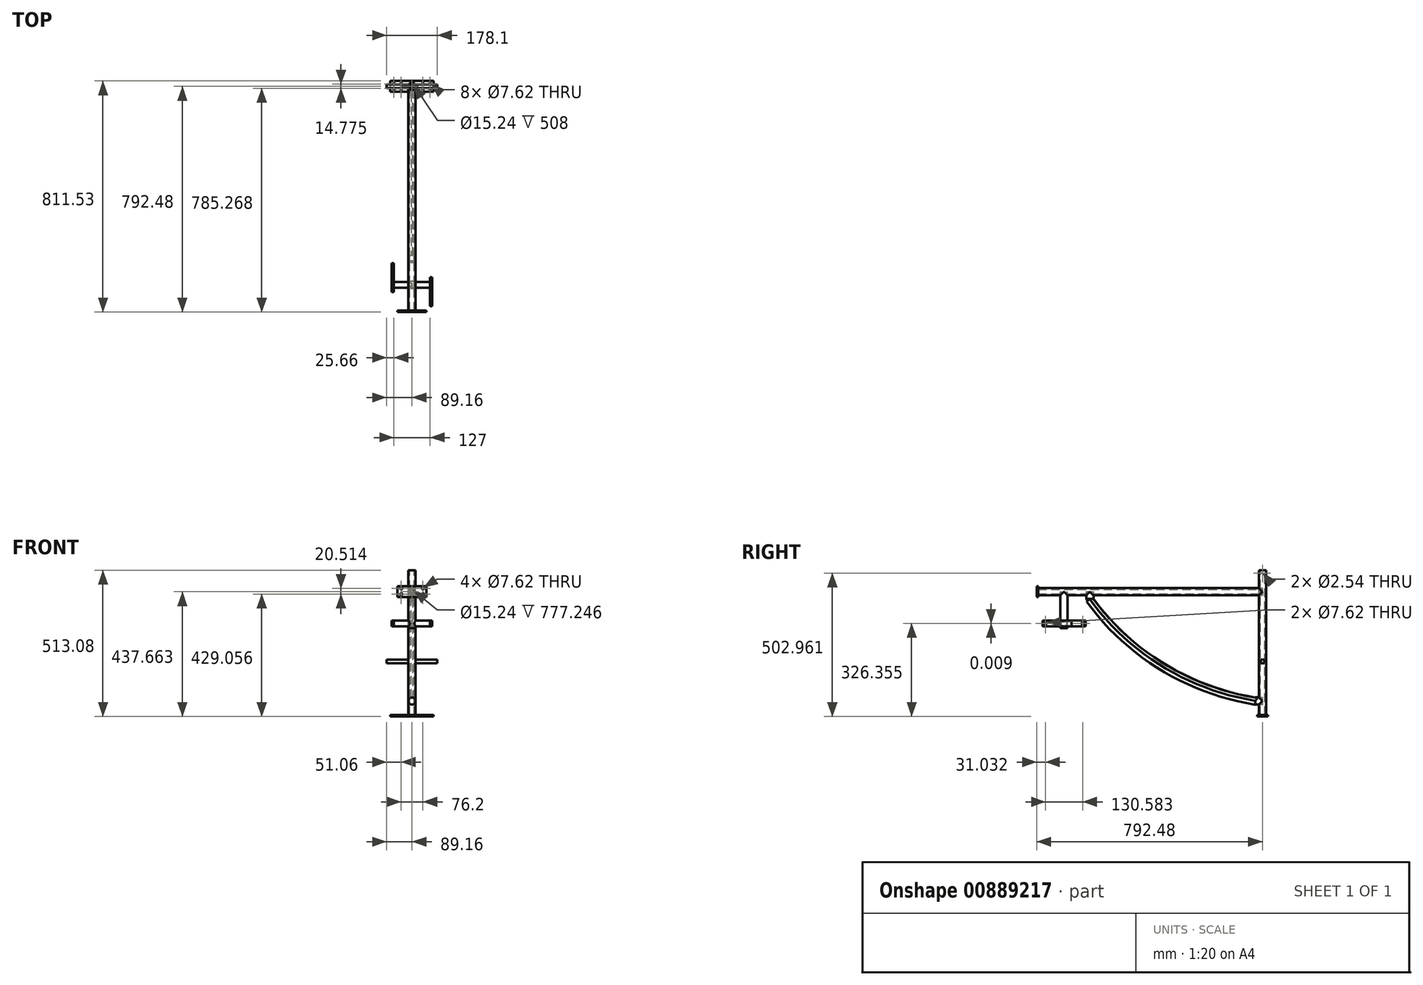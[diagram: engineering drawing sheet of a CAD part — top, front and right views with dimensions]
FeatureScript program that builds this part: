
annotation { "Feature Type Name" : "Feature", "Feature Type Description" : "" }
export const myFeature = defineFeature(function(context is Context, id is Id, definition is map)
    precondition{}
    {
        {
            var Q0;
            Q0=qCreatedBy(makeId("Top.planeOp"),FACE);
            var sketch = newSketch(context, id + "F0", { "sketchPlane" : qUnion([Q0])});
            skCircle(sketch, "E0", {"center": v(0, 0) * mm, "radius": 12.7 * mm});
            skCircle(sketch, "E1", {"center": v(0, 0) * mm, "radius": 7.62 * mm});
            skSolve(sketch);
        }
        {
            var Q0;
            Q0 = qSketchRegion(id + "F0", true);
            extrude(context, id + "F1", {"entities" : qUnion([Q0]), "oppositeDirection" : true, "depth" : 508 * mm, "offsetDistance" : 25.4 * mm});
        }
        {
            var Q0;
            Q0=qCreatedBy(makeId("Front.planeOp"),FACE);
            var sketch = newSketch(context, id + "F2", { "sketchPlane" : qUnion([Q0])});
            skCircle(sketch, "E2", {"center": v(0, -75.42) * mm, "radius": 7.62 * mm});
            skCircle(sketch, "E3", {"center": v(0, -75.42) * mm, "radius": 12.7 * mm});
            skSolve(sketch);
        }
        {
            var Q0;
            Q0 = qSketchRegion(id + "F2", true);
            extrude(context, id + "F3", {"entities" : qUnion([Q0]), "operationType" : NewBodyOperationType.ADD, "depth" : 787.4 * mm, "offsetDistance" : 25.4 * mm});
        }
        {
            var Q0;
            Q0=qCreatedBy(makeId("Front.planeOp"),FACE);
            var sketch = newSketch(context, id + "F4", { "sketchPlane" : qUnion([Q0])});
            skPoint(sketch, "E4", {"position": v(0, -459.21) * mm});
            skCircle(sketch, "E5", {"center": v(0, -459.21) * mm, "radius": 12.7 * mm});
            skSolve(sketch);
        }
        {
            var Q0;
            Q0=makeQuery(id+"F3.boolean.opBoolean","INTERSECT",VERTEX,{"disambiguationData":[OD(0.0)],"derivedFrom":[makeQuery(id+"F1.opExtrude","SWEPT_FACE",FACE,{"disambiguationData":[OSD([sQuery(id+"F0.wireOp",EDGE,"E0")])]}),makeQuery(id+"F3.opExtrude","SWEPT_FACE",FACE,{"disambiguationData":[OSD([sQuery(id+"F2.wireOp",EDGE,"E3")])]})]});
            var Q1;
            Q1=makeQuery(id+"F3.opExtrude","CAP_EDGE",EDGE,{"disambiguationData":[OSD([sQuery(id+"F2.wireOp",EDGE,"E2")])],"isStart":false});
            cPlane(context, id + "F5", {"entities" : qUnion([Q0, Q1]), "cplaneType" : CPlaneType.LINE_ANGLE, "offset" : 25.4 * mm, "angle" : 0 * degree, "width" : 152.4 * mm, "height" : 152.4 * mm});
        }
        {
            var Q0;
            Q0=qCreatedBy(id+"F5.planeOp",FACE);
            var sketch = newSketch(context, id + "F6", { "sketchPlane" : qUnion([Q0])});
            skCircle(sketch, "E6", {"center": v(0, 605.78) * mm, "radius": 12.7 * mm});
            skSolve(sketch);
        }
        {
            var Q0;
            Q0=qCreatedBy(makeId("Right.planeOp"),FACE);
            var sketch = newSketch(context, id + "F7", { "sketchPlane" : qUnion([Q0])});
            skPoint(sketch, "E7", {"position": v(0, -459.21) * mm});
            skPoint(sketch, "E8", {"position": v(-25.38, -459.21) * mm});
            skPoint(sketch, "E9", {"position": v(0, -75.19) * mm});
            skPoint(sketch, "E10", {"position": v(-608, -75.19) * mm});
            skPoint(sketch, "E11", {"position": v(-608, -101.57) * mm});
            skArc(sketch, "E12", {"start": v(-608, -101.57) * mm, "mid": v(-352.21, -338.26) * mm, "end": v(-25.38, -459.21) * mm});
            skSolve(sketch);
        }
        {
            var Q0;
            Q0 = qSketchRegion(id + "F6", true);
            extrude(context, id + "F8", {"entities" : qUnion([Q0]), "operationType" : NewBodyOperationType.ADD, "depth" : 25.4 * mm, "offsetDistance" : 25.4 * mm});
        }
        {
            var Q0;
            Q0 = qSketchRegion(id + "F4", true);
            extrude(context, id + "F9", {"entities" : qUnion([Q0]), "operationType" : NewBodyOperationType.ADD, "depth" : 25.4 * mm, "offsetDistance" : 25.4 * mm});
        }
        {
            var Q0;
            Q0=makeQuery(id+"F8.opExtrude","CAP_FACE",FACE,{"disambiguationData":[OSD([sQuery(id+"F6.wireOp",EDGE,"E6")])],"isStart":false});
            var Q1;
            Q1=makeQuery(id+"F9.opExtrude","CAP_FACE",FACE,{"disambiguationData":[OSD([sQuery(id+"F4.wireOp",EDGE,"E5")])],"isStart":false});
            var Q2;
            Q2=sQuery(id+"F7.wireOp",EDGE,"E12");
            sweep(context, id + "F10", {"operationType" : NewBodyOperationType.ADD, "profiles" : qUnion([Q0, Q1]), "path" : qUnion([Q2])});
        }
        {
            var Q0;
            Q0=makeQuery(id+"F1.opExtrude","CAP_FACE",FACE,{"disambiguationData":[OSD([sQuery(id+"F0.wireOp",EDGE,"E0"),sQuery(id+"F0.wireOp",EDGE,"E1")])],"isStart":false});
            cPlane(context, id + "F11", {"entities" : qUnion([Q0]), "cplaneType" : CPlaneType.OFFSET, "offset" : 0 * mm, "width" : 152.4 * mm, "height" : 152.4 * mm});
        }
        {
            var Q0;
            Q0=qCreatedBy(id+"F11.planeOp",FACE);
            var sketch = newSketch(context, id + "F12", { "sketchPlane" : qUnion([Q0])});
            skPoint(sketch, "E13", {"position": v(0, 0) * mm});
            skLineSegment(sketch, "E14.bottom", {"start": v(76.2, -19.05) * mm, "end": v(-76.2, -19.05) * mm});
            skLineSegment(sketch, "E14.top", {"start": v(76.2, 19.05) * mm, "end": v(-76.2, 19.05) * mm});
            skLineSegment(sketch, "E14.left", {"start": v(76.2, -19.05) * mm, "end": v(76.2, 19.05) * mm});
            skLineSegment(sketch, "E14.right", {"start": v(-76.2, -19.05) * mm, "end": v(-76.2, 19.05) * mm});
            skPoint(sketch, "E15", {"position": v(63.5, -7.56) * mm});
            skPoint(sketch, "E16", {"position": v(63.5, 7.21) * mm});
            skPoint(sketch, "E17", {"position": v(38.1, 7.21) * mm});
            skPoint(sketch, "E18", {"position": v(38.1, -7.56) * mm});
            skPoint(sketch, "E19", {"position": v(-38.1, -7.56) * mm});
            skPoint(sketch, "E20", {"position": v(-63.5, -7.56) * mm});
            skPoint(sketch, "E21", {"position": v(-63.5, 7.21) * mm});
            skPoint(sketch, "E22", {"position": v(-38.1, 7.21) * mm});
            skSolve(sketch);
        }
        {
            var Q0;
            Q0=makeQuery(id+"F12.imprint","IMPRINT",FACE,{"disambiguationData":[TD([[makeQuery(id+"F12.imprint","IMPRINT",EDGE,{"derivedFrom":sQuery(id+"F12.wireOp",EDGE,"E14.bottom")}),-1.0]])]});
            extrude(context, id + "F13", {"entities" : qUnion([Q0]), "operationType" : NewBodyOperationType.ADD, "depth" : 5.08 * mm, "offsetDistance" : 25.4 * mm});
        }
        {
            var Q0;
            Q0=sQuery(id+"F12.wireOp",VERTEX,"E21");
            var Q1;
            Q1=sQuery(id+"F12.wireOp",VERTEX,"E20");
            var Q2;
            Q2=sQuery(id+"F12.wireOp",VERTEX,"E19");
            var Q3;
            Q3=sQuery(id+"F12.wireOp",VERTEX,"E22");
            var Q4;
            Q4=sQuery(id+"F12.wireOp",VERTEX,"E17");
            var Q5;
            Q5=sQuery(id+"F12.wireOp",VERTEX,"E18");
            var Q6;
            Q6=sQuery(id+"F12.wireOp",VERTEX,"E15");
            var Q7;
            Q7=sQuery(id+"F12.wireOp",VERTEX,"E16");
            var Q8;
            Q8=makeQuery(id+"F1.opExtrude","SWEPT_BODY",BODY,{"disambiguationData":[OSD([sQuery(id+"F0.wireOp",EDGE,"E0"),sQuery(id+"F0.wireOp",EDGE,"E1")])]});
            hole(context, id + "F14", {"style" : HoleStyle.SIMPLE, "endStyle" : HoleEndStyle.THROUGH, "oppositeDirection" : true, "holeDiameter" : 7.62 * mm, "majorDiameter" : 6.35 * mm, "isTappedThrough" : true, "tappedDepth" : 12.7 * mm, "tapClearance" : 3, "locations" : qUnion([Q0, Q1, Q2, Q3, Q4, Q5, Q6, Q7]), "scope" : qUnion([Q8])});
        }
        {
            var Q0;
            Q0=qCreatedBy(makeId("Front.planeOp"),FACE);
            var sketch = newSketch(context, id + "F15", { "sketchPlane" : qUnion([Q0])});
            skPoint(sketch, "E23", {"position": v(0, -319.74) * mm});
            skPoint(sketch, "E24", {"position": v(-12.42, -319.74) * mm});
            skPoint(sketch, "E25", {"position": v(12.2, -319.74) * mm});
            skPoint(sketch, "E26", {"position": v(13.28, -319.74) * mm});
            skPoint(sketch, "E27", {"position": v(-13.5, -319.74) * mm});
            skSolve(sketch);
        }
        {
            var Q0;
            Q0=sQuery(id+"F15.wireOp",VERTEX,"E26");
            var Q1;
            Q1=sQuery(id+"F15.wireOp",VERTEX,"E25");
            cPlane(context, id + "F16", {"entities" : qUnion([Q0, Q1]), "cplaneType" : CPlaneType.MID_PLANE, "offset" : 25.4 * mm, "width" : 152.4 * mm, "height" : 152.4 * mm});
        }
        {
            var Q0;
            Q0=qCreatedBy(id+"F16.planeOp",FACE);
            var sketch = newSketch(context, id + "F17", { "sketchPlane" : qUnion([Q0])});
            skLineSegment(sketch, "E28.bottom", {"start": v(6.35, -313.56) * mm, "end": v(-6.35, -313.56) * mm});
            skLineSegment(sketch, "E28.top", {"start": v(6.35, -326.26) * mm, "end": v(-6.35, -326.26) * mm});
            skLineSegment(sketch, "E28.left", {"start": v(6.35, -313.56) * mm, "end": v(6.35, -326.26) * mm});
            skLineSegment(sketch, "E28.right", {"start": v(-6.35, -313.56) * mm, "end": v(-6.35, -326.26) * mm});
            skPoint(sketch, "E28.middle", {"position": v(0, -319.9) * mm});
            skSolve(sketch);
        }
        {
            var Q0;
            Q0=makeQuery(id+"F17.imprint","IMPRINT",FACE,{"disambiguationData":[TD([[makeQuery(id+"F17.imprint","IMPRINT",EDGE,{"derivedFrom":sQuery(id+"F17.wireOp",EDGE,"E28.bottom")}),1.0]])]});
            extrude(context, id + "F18", {"entities" : qUnion([Q0]), "oppositeDirection" : true, "depth" : 76.2 * mm, "offsetDistance" : 25.4 * mm});
        }
        {
            var Q0;
            Q0=makeQuery(id+"F18.opExtrude","CAP_FACE",FACE,{"disambiguationData":[OSD([sQuery(id+"F17.wireOp",EDGE,"E28.bottom"),sQuery(id+"F17.wireOp",EDGE,"E28.top"),sQuery(id+"F17.wireOp",EDGE,"E28.left"),sQuery(id+"F17.wireOp",EDGE,"E28.right")])],"isStart":false});
            cPlane(context, id + "F19", {"entities" : qUnion([Q0]), "cplaneType" : CPlaneType.OFFSET, "offset" : 0 * mm, "width" : 152.4 * mm, "height" : 152.4 * mm});
        }
        {
            var Q0;
            Q0=qCreatedBy(id+"F19.planeOp",FACE);
            var sketch = newSketch(context, id + "F20", { "sketchPlane" : qUnion([Q0])});
            skLineSegment(sketch, "E29", {"start": v(2.76, -319.8) * mm, "end": v(-136.94, -319.8) * mm, "construction": true});
            skLineSegment(sketch, "E30", {"start": v(-0.24, -319.8) * mm, "end": v(-0.24, -307.1) * mm});
            skLineSegment(sketch, "E31", {"start": v(-0.24, -307.1) * mm, "end": v(-132.32, -307.1) * mm});
            skLineSegment(sketch, "E32", {"start": v(-132.32, -307.1) * mm, "end": v(-132.32, -319.8) * mm});
            skSolve(sketch);
        }
        {
            var Q0;
            Q0=sQuery(id+"F15.wireOp",VERTEX,"E27");
            var Q1;
            Q1=sQuery(id+"F15.wireOp",VERTEX,"E24");
            cPlane(context, id + "F21", {"entities" : qUnion([Q0, Q1]), "cplaneType" : CPlaneType.MID_PLANE, "offset" : 25.4 * mm, "width" : 152.4 * mm, "height" : 152.4 * mm});
        }
        {
            var Q0;
            Q0=qCreatedBy(id+"F21.planeOp",FACE);
            var sketch = newSketch(context, id + "F22", { "sketchPlane" : qUnion([Q0])});
            skLineSegment(sketch, "E33.bottom", {"start": v(6.35, -313.4) * mm, "end": v(-6.35, -313.4) * mm});
            skLineSegment(sketch, "E33.top", {"start": v(6.35, -326.1) * mm, "end": v(-6.35, -326.1) * mm});
            skLineSegment(sketch, "E33.left", {"start": v(6.35, -313.4) * mm, "end": v(6.35, -326.1) * mm});
            skLineSegment(sketch, "E33.right", {"start": v(-6.35, -313.4) * mm, "end": v(-6.35, -326.1) * mm});
            skPoint(sketch, "E33.middle", {"position": v(0, -319.74) * mm});
            skSolve(sketch);
        }
        {
            var Q0;
            Q0=makeQuery(id+"F22.imprint","IMPRINT",FACE,{"disambiguationData":[TD([[makeQuery(id+"F22.imprint","IMPRINT",EDGE,{"derivedFrom":sQuery(id+"F22.wireOp",EDGE,"E33.bottom")}),1.0]])]});
            extrude(context, id + "F23", {"entities" : qUnion([Q0]), "oppositeDirection" : true, "depth" : 76.2 * mm, "offsetDistance" : 25.4 * mm});
        }
        {
            var Q0;
            Q0=makeQuery(id+"F23.opExtrude","CAP_FACE",FACE,{"disambiguationData":[OSD([sQuery(id+"F22.wireOp",EDGE,"E33.bottom"),sQuery(id+"F22.wireOp",EDGE,"E33.top"),sQuery(id+"F22.wireOp",EDGE,"E33.left"),sQuery(id+"F22.wireOp",EDGE,"E33.right")])],"isStart":false});
            cPlane(context, id + "F24", {"entities" : qUnion([Q0]), "cplaneType" : CPlaneType.OFFSET, "offset" : 0 * mm, "width" : 152.4 * mm, "height" : 152.4 * mm});
        }
        {
            var Q0;
            Q0=qCreatedBy(id+"F24.planeOp",FACE);
            var sketch = newSketch(context, id + "F25", { "sketchPlane" : qUnion([Q0])});
            skLineSegment(sketch, "E34", {"start": v(-3.49, -319.74) * mm, "end": v(136.21, -319.74) * mm, "construction": true});
            skLineSegment(sketch, "E35", {"start": v(132.08, -319.74) * mm, "end": v(132.08, -307.04) * mm});
            skLineSegment(sketch, "E36", {"start": v(132.08, -307.04) * mm, "end": v(0, -307.04) * mm});
            skLineSegment(sketch, "E37", {"start": v(0, -307.04) * mm, "end": v(0, -319.74) * mm});
            skSolve(sketch);
        }
        {
            var Q0;
            Q0=qCreatedBy(makeId("Right.planeOp"),FACE);
            var sketch = newSketch(context, id + "F26", { "sketchPlane" : qUnion([Q0])});
            skPoint(sketch, "E38", {"position": v(0, -10.12) * mm});
            skSolve(sketch);
        }
        {
            var Q0;
            Q0=sQuery(id+"F26.wireOp",VERTEX,"E38");
            var Q1;
            Q1=makeQuery(id+"F1.opExtrude","SWEPT_BODY",BODY,{"disambiguationData":[OSD([sQuery(id+"F0.wireOp",EDGE,"E0"),sQuery(id+"F0.wireOp",EDGE,"E1")])]});
            hole(context, id + "F27", {"style" : HoleStyle.SIMPLE, "endStyle" : HoleEndStyle.THROUGH, "holeDiameter" : 2.54 * mm, "majorDiameter" : 6.35 * mm, "isTappedThrough" : true, "tappedDepth" : 12.7 * mm, "tapClearance" : 3, "locations" : qUnion([Q0]), "scope" : qUnion([Q1])});
        }
        {
            var Q0;
            Q0=sQuery(id+"F26.wireOp",VERTEX,"E38");
            var Q1;
            Q1=makeQuery(id+"F1.opExtrude","SWEPT_BODY",BODY,{"disambiguationData":[OSD([sQuery(id+"F0.wireOp",EDGE,"E0"),sQuery(id+"F0.wireOp",EDGE,"E1")])]});
            hole(context, id + "F28", {"style" : HoleStyle.SIMPLE, "endStyle" : HoleEndStyle.THROUGH, "oppositeDirection" : true, "holeDiameter" : 2.54 * mm, "majorDiameter" : 6.35 * mm, "isTappedThrough" : true, "tappedDepth" : 12.7 * mm, "tapClearance" : 3, "locations" : qUnion([Q0]), "scope" : qUnion([Q1])});
        }
        {
            var Q0;
            Q0=qCreatedBy(makeId("Right.planeOp"),FACE);
            var sketch = newSketch(context, id + "F29", { "sketchPlane" : qUnion([Q0])});
            skPoint(sketch, "E39", {"position": v(0, -75.43) * mm});
            skPoint(sketch, "E40", {"position": v(-696.93, -75.43) * mm});
            skPoint(sketch, "E41", {"position": v(-696.93, -76.8) * mm});
            skPoint(sketch, "E42", {"position": v(-696.93, -186.66) * mm});
            skSolve(sketch);
        }
        {
            var Q0;
            Q0=sQuery(id+"F29.wireOp",VERTEX,"E40");
            var Q1;
            Q1=sQuery(id+"F29.wireOp",VERTEX,"E41");
            cPlane(context, id + "F30", {"entities" : qUnion([Q0, Q1]), "cplaneType" : CPlaneType.MID_PLANE, "offset" : 25.4 * mm, "width" : 152.4 * mm, "height" : 152.4 * mm});
        }
        {
            var Q0;
            Q0=qCreatedBy(id+"F30.planeOp",FACE);
            var sketch = newSketch(context, id + "F31", { "sketchPlane" : qUnion([Q0])});
            skCircle(sketch, "E43", {"center": v(0, 696.96) * mm, "radius": 12.7 * mm});
            skSolve(sketch);
        }
        {
            var Q0;
            Q0 = qSketchRegion(id + "F31", true);
            extrude(context, id + "F32", {"entities" : qUnion([Q0]), "operationType" : NewBodyOperationType.ADD, "depth" : 127 * mm, "offsetDistance" : 25.4 * mm});
        }
        {
            var Q0;
            Q0=makeQuery(id+"F3.opExtrude","CAP_FACE",FACE,{"disambiguationData":[OSD([sQuery(id+"F2.wireOp",EDGE,"E2"),sQuery(id+"F2.wireOp",EDGE,"E3")])],"isStart":false});
            cPlane(context, id + "F33", {"entities" : qUnion([Q0]), "cplaneType" : CPlaneType.OFFSET, "offset" : 0 * mm, "width" : 152.4 * mm, "height" : 152.4 * mm});
        }
        {
            var Q0;
            Q0=qCreatedBy(id+"F33.planeOp",FACE);
            var sketch = newSketch(context, id + "F34", { "sketchPlane" : qUnion([Q0])});
            skPoint(sketch, "E44.middle", {"position": v(0, -75.44) * mm});
            skLineSegment(sketch, "E45.bottom", {"start": v(-50.8, -56.39) * mm, "end": v(50.8, -56.39) * mm});
            skLineSegment(sketch, "E45.top", {"start": v(-50.8, -94.49) * mm, "end": v(50.8, -94.49) * mm});
            skLineSegment(sketch, "E45.left", {"start": v(-50.8, -56.39) * mm, "end": v(-50.8, -94.49) * mm});
            skLineSegment(sketch, "E45.right", {"start": v(50.8, -56.39) * mm, "end": v(50.8, -94.49) * mm});
            skPoint(sketch, "E46", {"position": v(-38.1, -63.51) * mm});
            skPoint(sketch, "E47", {"position": v(38.1, -63.51) * mm});
            skPoint(sketch, "E48", {"position": v(38.1, -84.02) * mm});
            skPoint(sketch, "E49", {"position": v(-38.1, -84.02) * mm});
            skSolve(sketch);
        }
        {
            var Q0;
            Q0=makeQuery(id+"F34.imprint","IMPRINT",FACE,{"disambiguationData":[TD([[makeQuery(id+"F34.imprint","IMPRINT",EDGE,{"derivedFrom":sQuery(id+"F34.wireOp",EDGE,"E45.bottom")}),-1.0]])]});
            extrude(context, id + "F35", {"entities" : qUnion([Q0]), "operationType" : NewBodyOperationType.ADD, "depth" : 5.08 * mm, "offsetDistance" : 25.4 * mm});
        }
        {
            var Q0;
            Q0=sQuery(id+"F34.wireOp",VERTEX,"E46");
            var Q1;
            Q1=sQuery(id+"F34.wireOp",VERTEX,"E47");
            var Q2;
            Q2=sQuery(id+"F34.wireOp",VERTEX,"E48");
            var Q3;
            Q3=sQuery(id+"F34.wireOp",VERTEX,"E49");
            var Q4;
            Q4=makeQuery(id+"F1.opExtrude","SWEPT_BODY",BODY,{"disambiguationData":[OSD([sQuery(id+"F0.wireOp",EDGE,"E0"),sQuery(id+"F0.wireOp",EDGE,"E1")])]});
            hole(context, id + "F36", {"style" : HoleStyle.SIMPLE, "endStyle" : HoleEndStyle.THROUGH, "oppositeDirection" : true, "holeDiameter" : 7.62 * mm, "majorDiameter" : 6.35 * mm, "isTappedThrough" : true, "tappedDepth" : 12.7 * mm, "tapClearance" : 3, "locations" : qUnion([Q0, Q1, Q2, Q3]), "scope" : qUnion([Q4])});
        }
        {
            var Q0;
            Q0=qCreatedBy(makeId("Right.planeOp"),FACE);
            var sketch = newSketch(context, id + "F37", { "sketchPlane" : qUnion([Q0])});
            skCircle(sketch, "E50", {"center": v(-696.85, -186.7) * mm, "radius": 10.16 * mm});
            skSolve(sketch);
        }
        {
            var Q0;
            Q0=sQuery(id+"F29.wireOp",VERTEX,"E42");
            var Q1;
            Q1=makeQuery(id+"F1.opExtrude","SWEPT_BODY",BODY,{"disambiguationData":[OSD([sQuery(id+"F0.wireOp",EDGE,"E0"),sQuery(id+"F0.wireOp",EDGE,"E1")])]});
            hole(context, id + "F38", {"style" : HoleStyle.SIMPLE, "endStyle" : HoleEndStyle.THROUGH, "holeDiameter" : 20.32 * mm, "majorDiameter" : 6.35 * mm, "isTappedThrough" : true, "tappedDepth" : 12.7 * mm, "tapClearance" : 3, "locations" : qUnion([Q0]), "scope" : qUnion([Q1])});
        }
        {
            var Q0;
            Q0=sQuery(id+"F37.wireOp",VERTEX,"E50.center");
            var Q1;
            Q1=makeQuery(id+"F1.opExtrude","SWEPT_BODY",BODY,{"disambiguationData":[OSD([sQuery(id+"F0.wireOp",EDGE,"E0"),sQuery(id+"F0.wireOp",EDGE,"E1")])]});
            hole(context, id + "F39", {"style" : HoleStyle.SIMPLE, "endStyle" : HoleEndStyle.THROUGH, "oppositeDirection" : true, "holeDiameter" : 20.32 * mm, "majorDiameter" : 6.35 * mm, "isTappedThrough" : true, "tappedDepth" : 12.7 * mm, "tapClearance" : 3, "locations" : qUnion([Q0]), "scope" : qUnion([Q1])});
        }
        {
            var Q0;
            Q0 = qSketchRegion(id + "F37", true);
            extrude(context, id + "F40", {"entities" : qUnion([Q0]), "operationType" : NewBodyOperationType.ADD, "endBound" : BoundingType.SYMMETRIC, "depth" : 127 * mm, "offsetDistance" : 25.4 * mm});
        }
        {
            var Q0;
            Q0=makeQuery(id+"F40.opExtrude","CAP_FACE",FACE,{"disambiguationData":[OSD([sQuery(id+"F37.wireOp",EDGE,"E50")])],"isStart":false});
            cPlane(context, id + "F41", {"entities" : qUnion([Q0]), "cplaneType" : CPlaneType.OFFSET, "offset" : 0 * mm, "width" : 152.4 * mm, "height" : 152.4 * mm});
        }
        {
            var Q0;
            Q0=qCreatedBy(id+"F41.planeOp",FACE);
            var sketch = newSketch(context, id + "F42", { "sketchPlane" : qUnion([Q0])});
            skLineSegment(sketch, "E51.bottom", {"start": v(-771.6, -176.57) * mm, "end": v(-670, -176.57) * mm});
            skLineSegment(sketch, "E51.top", {"start": v(-771.6, -196.89) * mm, "end": v(-670, -196.89) * mm});
            skLineSegment(sketch, "E51.left", {"start": v(-771.6, -176.57) * mm, "end": v(-771.6, -196.89) * mm});
            skLineSegment(sketch, "E51.right", {"start": v(-670, -176.57) * mm, "end": v(-670, -196.89) * mm});
            skPoint(sketch, "E52", {"position": v(-761.45, -186.73) * mm});
            skPoint(sketch, "E52.positionSnap0", {"position": v(-771.6, -186.73) * mm});
            skSolve(sketch);
        }
        {
            var Q0;
            Q0=makeQuery(id+"F42.imprint","IMPRINT",FACE,{"disambiguationData":[TD([[makeQuery(id+"F42.imprint","IMPRINT",EDGE,{"derivedFrom":sQuery(id+"F42.wireOp",EDGE,"E51.bottom")}),-1.0]])]});
            extrude(context, id + "F43", {"entities" : qUnion([Q0]), "operationType" : NewBodyOperationType.ADD, "depth" : 7.62 * mm, "offsetDistance" : 25.4 * mm});
        }
        {
            var Q0;
            Q0=sQuery(id+"F42.wireOp",VERTEX,"E52");
            var Q1;
            Q1=makeQuery(id+"F1.opExtrude","SWEPT_BODY",BODY,{"disambiguationData":[OSD([sQuery(id+"F0.wireOp",EDGE,"E0"),sQuery(id+"F0.wireOp",EDGE,"E1")])]});
            hole(context, id + "F44", {"style" : HoleStyle.SIMPLE, "endStyle" : HoleEndStyle.THROUGH, "oppositeDirection" : true, "holeDiameter" : 7.62 * mm, "majorDiameter" : 6.35 * mm, "isTappedThrough" : true, "tappedDepth" : 12.7 * mm, "tapClearance" : 3, "locations" : qUnion([Q0]), "scope" : qUnion([Q1])});
        }
        {
            var Q0;
            Q0=makeQuery(id+"F40.opExtrude","CAP_FACE",FACE,{"disambiguationData":[OSD([sQuery(id+"F37.wireOp",EDGE,"E50")])],"isStart":true});
            cPlane(context, id + "F45", {"entities" : qUnion([Q0]), "cplaneType" : CPlaneType.OFFSET, "offset" : 0 * mm, "width" : 152.4 * mm, "height" : 152.4 * mm});
        }
        {
            var Q0;
            Q0=qCreatedBy(id+"F45.planeOp",FACE);
            var sketch = newSketch(context, id + "F46", { "sketchPlane" : qUnion([Q0])});
            skPoint(sketch, "E53.positionSnap0", {"position": v(773.1, -186.72) * mm});
            skLineSegment(sketch, "E54.MirrorCS", {"start": v(696.9, -176.56) * mm, "end": v(620.7, -176.56) * mm});
            skLineSegment(sketch, "E55.MirrorCS", {"start": v(620.7, -176.56) * mm, "end": v(620.7, -196.88) * mm});
            skPoint(sketch, "E56.MirrorP", {"position": v(630.86, -186.72) * mm});
            skLineSegment(sketch, "E57.MirrorCS", {"start": v(696.9, -196.88) * mm, "end": v(620.7, -196.88) * mm});
            skLineSegment(sketch, "E58", {"start": v(722.3, -176.56) * mm, "end": v(722.3, -196.88) * mm});
            skLineSegment(sketch, "E59", {"start": v(696.9, -176.56) * mm, "end": v(722.3, -176.56) * mm});
            skLineSegment(sketch, "E60", {"start": v(696.9, -196.88) * mm, "end": v(722.3, -196.88) * mm});
            skSolve(sketch);
        }
        {
            var Q0;
            Q0=makeQuery(id+"F46.imprint","IMPRINT",FACE,{"disambiguationData":[TD([[makeQuery(id+"F46.imprint","IMPRINT",EDGE,{"derivedFrom":sQuery(id+"F46.wireOp",EDGE,"E54.MirrorCS")}),1.0]])]});
            extrude(context, id + "F47", {"entities" : qUnion([Q0]), "operationType" : NewBodyOperationType.ADD, "depth" : 7.62 * mm, "offsetDistance" : 25.4 * mm});
        }
        {
            var Q0;
            Q0=sQuery(id+"F46.wireOp",VERTEX,"E56.MirrorP");
            var Q1;
            Q1=makeQuery(id+"F1.opExtrude","SWEPT_BODY",BODY,{"disambiguationData":[OSD([sQuery(id+"F0.wireOp",EDGE,"E0"),sQuery(id+"F0.wireOp",EDGE,"E1")])]});
            hole(context, id + "F48", {"style" : HoleStyle.SIMPLE, "endStyle" : HoleEndStyle.THROUGH, "oppositeDirection" : true, "holeDiameter" : 7.62 * mm, "majorDiameter" : 6.35 * mm, "isTappedThrough" : true, "tappedDepth" : 12.7 * mm, "tapClearance" : 3, "locations" : qUnion([Q0]), "scope" : qUnion([Q1])});
        }
        {
            var Q0;
            Q0=sQuery(id+"F20.wireOp",EDGE,"E31");
            var Q1;
            Q1=sQuery(id+"F20.wireOp",EDGE,"E29");
            revolve(context, id + "F49", {"bodyType" : ToolBodyType.SURFACE, "surfaceOperationType" : NewSurfaceOperationType.NEW, "surfaceEntities" : qUnion([Q0]), "axis" : qUnion([Q1]), "revolveType" : RevolveType.FULL});
        }
        {
            var Q0;
            Q0=sQuery(id+"F25.wireOp",EDGE,"E36");
            var Q1;
            Q1=sQuery(id+"F25.wireOp",EDGE,"E34");
            revolve(context, id + "F50", {"bodyType" : ToolBodyType.SURFACE, "surfaceOperationType" : NewSurfaceOperationType.NEW, "surfaceEntities" : qUnion([Q0]), "axis" : qUnion([Q1]), "revolveType" : RevolveType.FULL});
        }
    });
